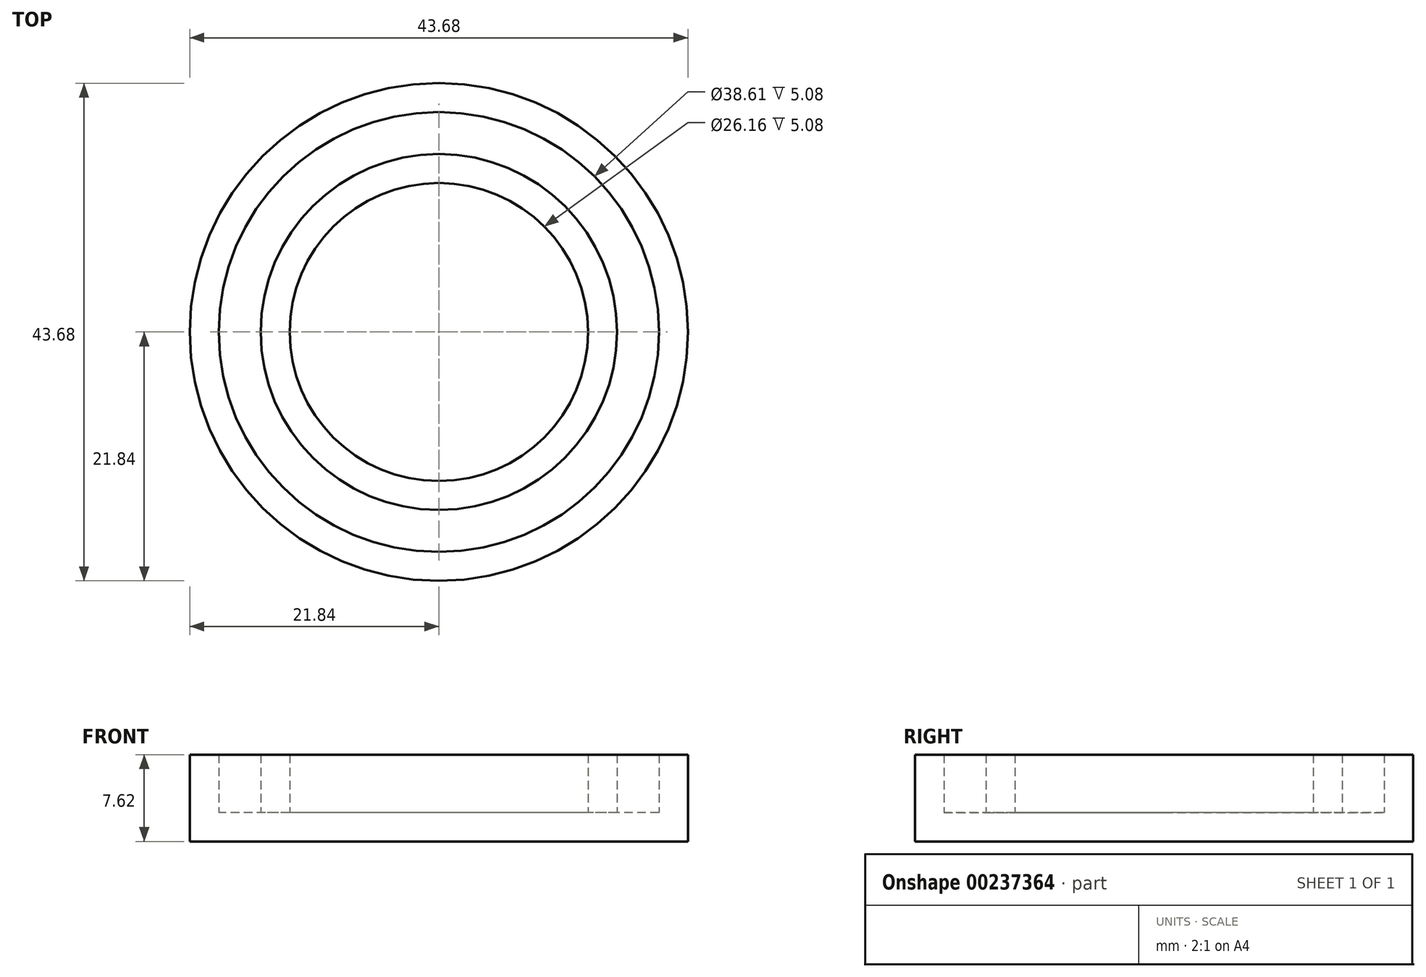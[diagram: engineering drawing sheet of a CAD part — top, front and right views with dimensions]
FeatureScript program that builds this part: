
annotation { "Feature Type Name" : "Feature", "Feature Type Description" : "" }
export const myFeature = defineFeature(function(context is Context, id is Id, definition is map)
    precondition{}
    {
        {
            var Q0;
            Q0=qCreatedBy(makeId("Top.planeOp"),FACE);
            var sketch = newSketch(context, id + "F0", { "sketchPlane" : qUnion([Q0])});
            skCircle(sketch, "E0", {"center": v(0, 0) * mm, "radius": 15.62 * mm, "construction": true});
            skCircle(sketch, "E1", {"center": v(0, 0) * mm, "radius": 19.3 * mm, "construction": true});
            skCircle(sketch, "E2", {"center": v(0, 0) * mm, "radius": 21.84 * mm});
            skLineSegment(sketch, "E3", {"start": v(19.3, 0) * mm, "end": v(21.84, 0) * mm, "construction": true});
            skSolve(sketch);
        }
        {
            var Q0;
            Q0 = qSketchRegion(id + "F0", true);
            extrude(context, id + "F1", {"entities" : qUnion([Q0]), "depth" : 2.54 * mm});
        }
        {
            var Q0;
            Q0=makeQuery(id+"F1.opExtrude","CAP_FACE",FACE,{"disambiguationData":[OSD([sQuery(id+"F0.wireOp",EDGE,"E2")])],"isStart":false});
            var sketch = newSketch(context, id + "F2", { "sketchPlane" : qUnion([Q0])});
            skCircle(sketch, "E4", {"center": v(0, 0) * mm, "radius": 21.84 * mm});
            skCircle(sketch, "E5", {"center": v(0, 0) * mm, "radius": 19.3 * mm});
            skSolve(sketch);
        }
        {
            var Q0;
            Q0=makeQuery(id+"F1.opExtrude","CAP_FACE",FACE,{"disambiguationData":[OSD([sQuery(id+"F0.wireOp",EDGE,"E2")])],"isStart":false});
            var sketch = newSketch(context, id + "F3", { "sketchPlane" : qUnion([Q0])});
            skCircle(sketch, "E6", {"center": v(0, 0) * mm, "radius": 13.08 * mm});
            skCircle(sketch, "E7", {"center": v(0, 0) * mm, "radius": 15.62 * mm});
            skLineSegment(sketch, "E8", {"start": v(13.08, 0) * mm, "end": v(15.62, 0) * mm, "construction": true});
            skSolve(sketch);
        }
        {
            var Q0;
            Q0 = qSketchRegion(id + "F2", true);
            var Q1;
            Q1 = qSketchRegion(id + "F3", true);
            extrude(context, id + "F4", {"entities" : qUnion([Q0, Q1]), "operationType" : NewBodyOperationType.ADD, "depth" : 5.08 * mm});
        }
    });
